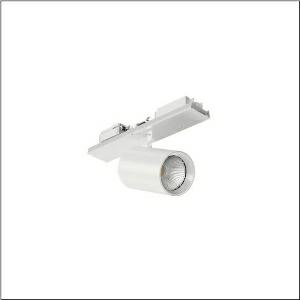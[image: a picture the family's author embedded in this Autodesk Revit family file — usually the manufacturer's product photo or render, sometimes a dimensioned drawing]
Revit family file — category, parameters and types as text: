
# Revit family: licross_spot_31_51sl137a43b
name_source: partatom
category: Lighting Fixtures
units: mm (PartAtom-declared; Revit-internal decimal feet)

## family parameters
Cut with Voids When Loaded = No
Host = Face
Light Source = No
Part Type = Normal
Room Calculation Point = No
Round Connector Dimension = Use Diameter
Shared = No

## types (1)
- --- (1 x LED, 3680 lm, 28 W, 4000K)
    Apparent Load = 28 VA
    CIE Flux Codes = 92 97 99 100 100
    Color Rendering = 90
    Color Temperature = 4000K
    Default Elevation = 1800 mm
    Description = Licross Spot 31, directional spotlight, light control with lens, of plastic, LED rated luminous flux: 3.680lm, light colour: 940, with plug, 3-pole, with phase selection, mains connection: 220..240V, AC, 50/60Hz, of aluminium, traffic white (RAL 9016), length: 300mm, diameter: 90mm, protection rating (complete): IP20, insulation class (complete): insulation class I (protective earthing), certification: CE, packaging unit: 1 piece
    Height = 175 mm
    Lamp = 1 x LED
    Lamp Light Flux = 3680 lm
    Lamp Power = 28 W
    Lamp count = 1
    Length = 90 mm
    Luminous efficacy = 131 lm/W
    Manufacturer = Siteco
    ModVariant = No
    Model = 51SL137A43B
    Mounting Place = Ceiling
    Mounting Type = Pendant
    Number of Poles = 1
    OnlyDefault = Yes
    Power Factor = 1
    Product Name = Licross Spot 31
    Product group = directional spotlight
    ProductGroupID = 905
    Protection Class = Protection class I
    Protection Degree = IP 20
    RLX_Detail_Level = 1
    RLX_Emergency_Light_Flux = 0 lm
    RLX_Emergency_Type = 0
    RLX_Emergency_Type_DB = No
    RlxData = <blob elided: 14865 chars, md5=d7aff5f1>
    Socket = socket
    Standby Power = 0 W
    System Light Flux = 3680 lm
    System Power = 28 W
    Type Comments = factory setting: luminous flux: 100 % | (ON | ON | ON) | 700 mA
    Type Image = l_1245720.jpg
    URL = http://relux.com
    VarID = @adj_131961
    Voltage = 0 V
    Weight = 0.00 kg
    Width = 0 mm  [stored 0 ft]

note: [stored X ft] marks values corroborated as IEEE doubles in the binary element streams (Revit-internal decimal feet)

## geometry (parser evidence)
native form markers: Sweep x11
no freeform markers — native parametric forms only
